FCSTD DOCUMENT  (FreeCAD 0.16RUnknown)
Label: servoAxis
License: All rights reserved
LicenseURL: http://en.wikipedia.org/wiki/All_rights_reserved
objects: Part::Part2DObjectPython×5, App::MeasureDistance×2, Spreadsheet::Sheet×1
note: 5 computed .brp shape members not serialized (recipe doc carries the construction recipe); baked Part::Feature solids carry a one-line shape summary decoded from their .brp

FEATURE [Part::Part2DObjectPython] Rectangle  # Draft 2D object (typed FeaturePython)
  ChamferSize = 0
  Columns = 1
  FilletRadius = 4
  Height = 10
  Length = 76.5
  MakeFace = true
  Rows = 1
  expr: FilletRadius = prefs.fillet
  expr: Length = prefs.servoAxis + prefs.length + 2 * prefs.holeDistance
  expr: Height = prefs.width
FEATURE [Spreadsheet::Sheet] Spreadsheet  label="prefs"
  cells = A1=servo axis length (for screws); B1(servoAxis)=16.5; C1=mm; D1=name = servoAxis; A2=length from rotation point; B2(length)=50; C2=mm; D2=name = length; A3=width; B3(width)=10; C3=mm; D3=name = width; A4=hole radius; B4(holeRadius)=1; C4=mm; D4=name = holeRadius; A5=distance from holes to borders; B5(holeDistance)=5; C5=mm; D5=name = holeDistance; A6=rectangle vertex fillet radius; B6(fillet)=4; C6=mm; D6=name = fillet
FEATURE [Part::Part2DObjectPython] Circle  # Draft 2D object (typed FeaturePython)
  FirstAngle = 0
  LastAngle = 0
  MakeFace = true
  Placement = pos=(21.5,5,0) rot=(0,0,1;0rad)
  Radius = 0.5
  expr: Placement.Base.y = prefs.width / 2
  expr: Placement.Base.x = prefs.servoAxis + prefs.holeDistance
FEATURE [Part::Part2DObjectPython] Circle001  label="axisHole"  # Draft 2D object (typed FeaturePython)
  FirstAngle = 0
  LastAngle = 0
  MakeFace = true
  Placement = pos=(5,5,0) rot=(0,0,1;0rad)
  Radius = 1
  expr: Placement.Base.y = prefs.width / 2
  expr: Placement.Base.x = prefs.holeDistance
FEATURE [Part::Part2DObjectPython] Circle002  label="axisHole2"  # Draft 2D object (typed FeaturePython)
  FirstAngle = 0
  LastAngle = 0
  MakeFace = true
  Placement = pos=(38,5,0) rot=(0,0,1;0rad)
  Radius = 1
  expr: Placement.Base.y = prefs.width / 2
  expr: Placement.Base.x = prefs.holeDistance + 2 * prefs.servoAxis
FEATURE [Part::Part2DObjectPython] Circle003  label="axisHole3"  # Draft 2D object (typed FeaturePython)
  FirstAngle = 0
  LastAngle = 0
  MakeFace = true
  Placement = pos=(71.5,5,0) rot=(0,0,1;0rad)
  Radius = 1
  expr: Placement.Base.y = prefs.width / 2
  expr: Placement.Base.x = prefs.holeDistance + prefs.servoAxis + prefs.length
FEATURE [App::MeasureDistance] Distance  label="Distance: 76.5002 mm"
  Distance = 76.5
  P1 = (0,0,0)
  P2 = (76.5,0,0)
FEATURE [App::MeasureDistance] Distance001  label="Distance: 10.0196 mm"
  Distance = 10
  P1 = (0,0,0)
  P2 = (0,10,0)
